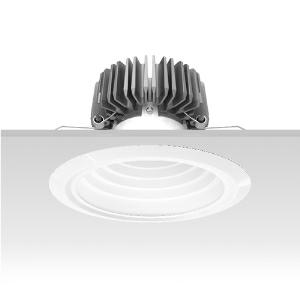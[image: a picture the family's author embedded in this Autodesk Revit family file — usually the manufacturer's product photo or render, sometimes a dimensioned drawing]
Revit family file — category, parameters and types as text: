
# Revit family: 3f_filippi_-_3f_reno_bianco_ampio_3f_filippi_-_30683_a01025_-_3f_reno_200_wh_3000-930_dali_wide___vt_wh_3ed5
name_source: partatom
category: Lighting Fixtures
units: mm (PartAtom-declared; Revit-internal decimal feet)

## family parameters
Cut with Voids When Loaded = No
Host = Face
Light Source = No
Part Type = Normal
Room Calculation Point = No
Round Connector Dimension = Use Diameter
Shared = No

## types (1)
- 3F Filippi - 3F Reno Bianco Ampio (1 x LED, 2537 lm, 37 W, 3000 K)
    Apparent Load = 37 VA
    Approval mark = CE
    CIE Flux Codes = 75 94 99 100 100
    Color Rendering = 90
    Color Temperature = 3000 K
    Control Gear = Electronic transformer
    Default Elevation = 1800 mm
    Description = ILLUMINOTECHNICAL
Luminous efficiency 100% (DLOR 100%, ULOR 0%).
Initial luminous flux of the luminaire 2537 lm.
Direct symmetric wide distribution.
Installation Interdistance Transv.D = 1.56 x hu - Long.D = 1.56 x hu.
Tabular UGR (CIE 117 - 4H-8H; S=0.25H; 70/50/20): RUG 21.8 - 21.7.
Beam angle: 74° - 74°.
Luminous efficacy 69 lm/W.
Lifetime (L90/B10): 30000 h. (tq+25°C)
Lifetime (L85/B10): 50000 h. (tq+25°C)
Lifetime (L70/B10): 80000 h. (tq+25°C)
Sudden decreased luminous flux after 50000 hours: 0% (C0).
Photobiological safety in compliance with IEC/TR 62778: RG0 risk exempt, (IEC 62471).
In compliance with IEC/EN 62722-2-1 - IEC/EN 62717 standards.

SOURCE
Compact LED module 3000/930.
Energy efficiency class (UE 2019/2020 - UE 2019/2015): E.
CIE 13.3 Colour rendering index: CRI >90 (R9 >50%).
IES TM-30 Fidelity Index: Rf = 92 Rg = 101.
CCT nominal colour temperature 3000 K.
Colour initial tolerance (MacAdam): SDCM 3.
Zhaga Book 3 compliant.

MECHANICAL
Passive heat dissipator in die-casting aluminium, oversized, for optimum thermal management of the LED module.
Parabolic element with graduated/concentric rings in white polycarbonate.
Transparent external lens with glossy and satin differentiated surfaces, with a cooling and anti-insect system in methacrylate (PMMA).
Fastening spring clips in stainless steel.
Dimensions: diameter 226 mm, height 146 mm. Weight 1.755 kg.
IP44 protection degree for exposed part, IP20 for recessed part.
Mechanical strength to impacts IK06 (1 joule).
Glow-wire test resistance 650°C.

ELECTRICAL
Wiring on a separate unit.
Halogen Free DALI-2 DATI (Parts 251, 252, 253), PUSH-DIM, electronic wiring 230V-50/60Hz, power factor 0.97 at full load, THD <25%, constant output current, SELV, class II, 1 driver, 1 DALI addresse.
Power of the luminaire 37 W.
ENEC - CE.
SAFE FLICKER: PstLM=<1 and SVM=<0.4 (IEC TR 61547-1 and IEC TR 63158), to ensure a more comfortable and safe light.
Luminaire compliant with EN 60598-2-22 for power supply from a centralised emergency system CPSS (Central Power Supply System), not incorporated in the luminaire - high risk areas excluded. The default power and flux are 100% in AC and 100% in DC.
Ambient temperature from 0°C to +25°C.
Temperature class T6 max 85°C.
Relative humidity UR: <85%.

INSTALLATION
Pull-up recessed fitting.
False ceiling carving: 200 mm.
All accessories dedicated to this product are available on the Catalog and on our website www.3F-Filippi.com.

ACCESSORIES
A01025 - VT transparent glass, tempered, not flammable, locked and in line with the trim, in white polycarbonate.

APPLICATIONS
Environments: architectural, commercial, exhibition areas, transit areas, corridors, shops, display windows, service areas.
In false ceilings with narrow voids.

LIGHT MANAGEMENT
Recommended minimum setting: 10%.
The luminaire, equipped with (DALI-2 DATI) driver, can be controlled manually with 3F Easy Dim technology or automatically/manually with wired or wireless DALI/D2D control systems.
The D2D driver guarantees interoperability with other devices with the same certification by making the following information available:
Device Data (Part 251), Energy Report (Part 252), Diagnosis & Maintenance (Part 253).
In electrical systems without a regulation system (manual or automatic) and DALI bus, a suitable jumper must be made on the DA-DA terminals of the appliance.

WARNING
Luminaire designed for disposal/recycling at end-of-life.
Replaceable (LED only) light source by a professional. Replaceable control gear by a professional.
    Height = 0 mm  [stored 0 ft]
    Lamp = 1 x LED
    Lamp Light Flux = 2537 lm
    Lamp Power = 37 W
    Lamp count = 1
    Length = 226 mm
    Lifetime = 50000 h
    Luminous efficacy = 69 lm/W
    Manufacturer = 3F Filippi
    ModVariant = No
    Model = 3F Filippi - 30683+A01025 - 3F Reno 200 WH 3000-930 DALI WIDE + VT WH
    Mounting Place = Ceiling
    Mounting Type = Recessed
    Number of Poles = 1
    OnlyDefault = Yes
    Power Factor = 1
    Product Name = 3F Filippi - 3F Reno Bianco Ampio
    Product group = recessed luminaire
    ProductGroupID = 4
    Protection Class = Protection class II
    Protection Degree = IP 20
    RLX_Detail_Level = 1
    RLX_Emergency_Light_Flux = 0 lm
    RLX_Emergency_Type = 0
    RLX_Emergency_Type_DB = No
    RlxData = <blob elided: 98125 chars, md5=d536d226>
    Socket = socket
    Standby Power = 0 W
    System Light Flux = 2537 lm
    System Power = 37 W
    Type Comments = Product without accessories
    Type Image = 3ffilippi_3f_reno_200_wh__a01025.jpg
    URL = http://relux.com
    VarID = ---
    Voltage = 0 V
    Weight = 0.00 kg
    Width = 0 mm  [stored 0 ft]

note: [stored X ft] marks values corroborated as IEEE doubles in the binary element streams (Revit-internal decimal feet)

## geometry (parser evidence)
native form markers: Blend x4, Sweep x11
no freeform markers — native parametric forms only
